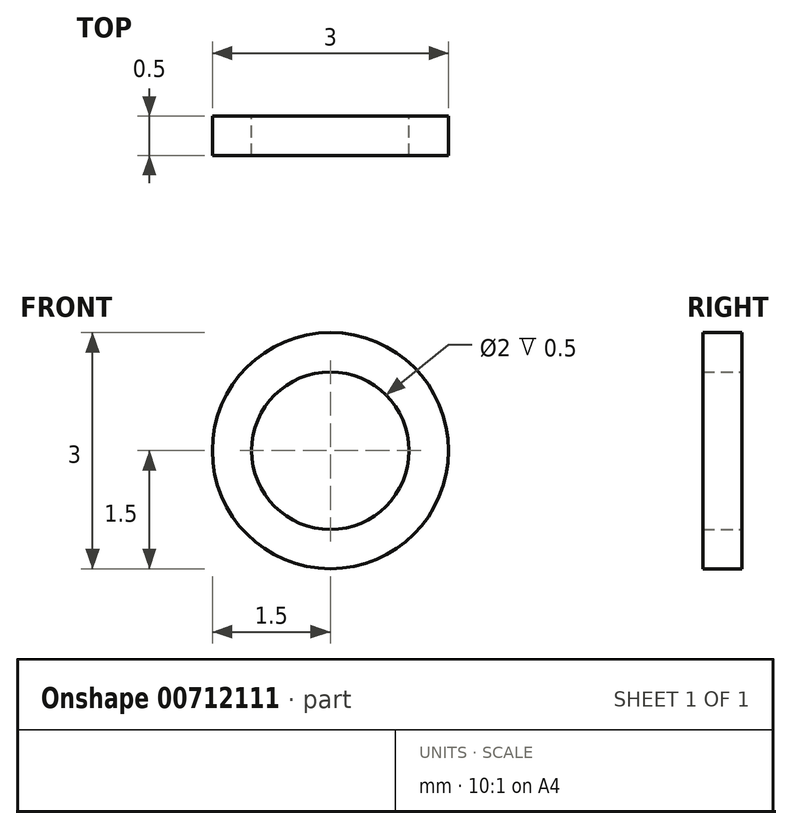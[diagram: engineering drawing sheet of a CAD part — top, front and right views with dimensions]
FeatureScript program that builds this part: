
annotation { "Feature Type Name" : "Feature", "Feature Type Description" : "" }
export const myFeature = defineFeature(function(context is Context, id is Id, definition is map)
    precondition{}
    {
        {
            var Q0;
            Q0=qCreatedBy(makeId("Front.planeOp"),FACE);
            var sketch = newSketch(context, id + "F0", { "sketchPlane" : qUnion([Q0])});
            skCircle(sketch, "E0", {"center": v(0, 0) * mm, "radius": 1.5 * mm});
            skCircle(sketch, "E1", {"center": v(0, 0) * mm, "radius": 1 * mm});
            skSolve(sketch);
        }
        {
            var Q0;
            Q0=makeQuery(id+"F0.imprint","IMPRINT",FACE,{"disambiguationData":[TD([[makeQuery(id+"F0.imprint","IMPRINT",EDGE,{"derivedFrom":sQuery(id+"F0.wireOp",EDGE,"E0")}),1.0]])]});
            extrude(context, id + "F1", {"entities" : qUnion([Q0]), "depth" : .5 * mm, "offsetDistance" : 25 * mm});
        }
    });
